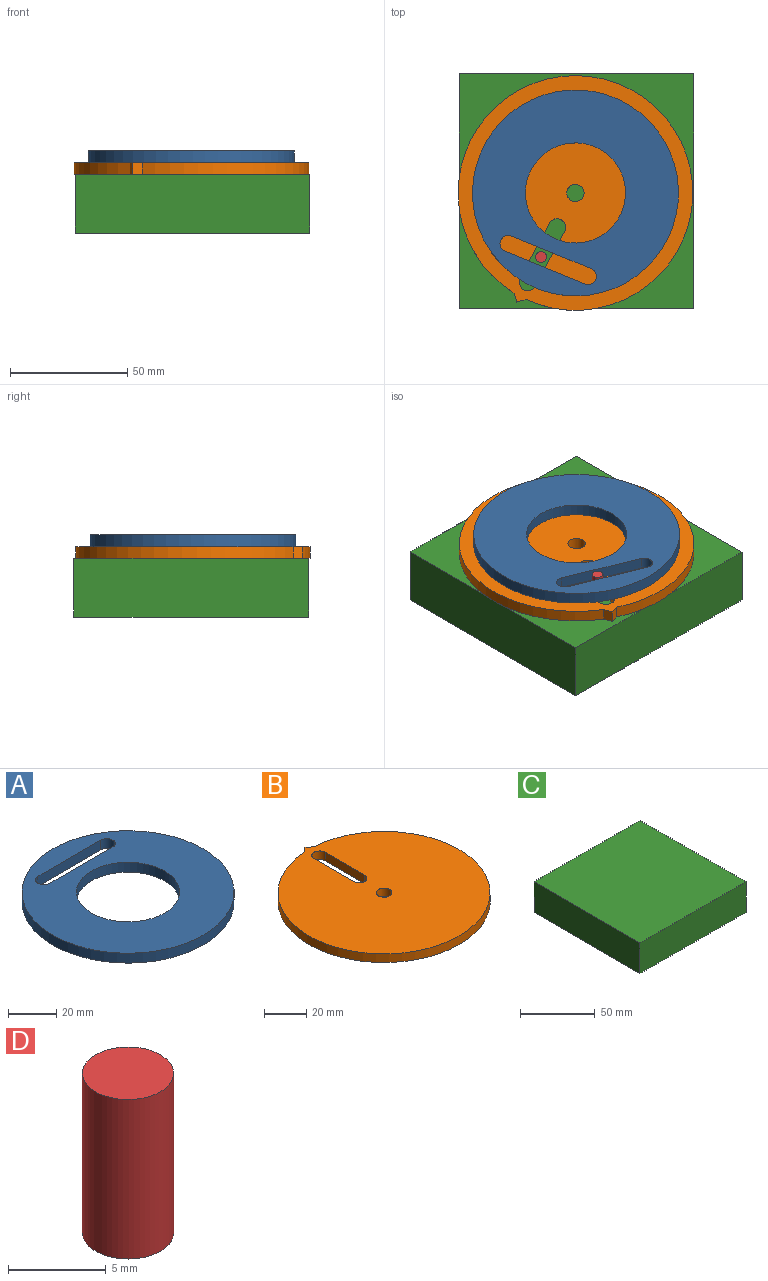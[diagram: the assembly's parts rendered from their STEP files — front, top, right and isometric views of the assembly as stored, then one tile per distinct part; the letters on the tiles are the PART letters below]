
ASSEMBLY  parts=4 mates=4
PART A: 8 faces, bbox 87.7x87.7x5 mm
  f0: cylinder r=3.5mm len=7mm, axis (0,0,-1), area 55mm2, adj f1,f4,f6,f7
  f1: plane 36.75x5mm, normal (0,-1,0), area 183.7mm2, adj f0,f2,f6,f7
  f2: cylinder r=3.5mm len=7mm, axis (0,0,-1), area 55mm2, adj f1,f4,f6,f7
  f3: cylinder r=43.87mm len=87.75mm, axis (0,0,-1), area 1378.3mm2, adj f6,f7
  f4: plane 36.75x5mm, normal (0,1,0), area 183.7mm2, adj f0,f2,f6,f7
  f5: cylinder r=21.33mm len=42.67mm, axis (0,0,-1), area 670.2mm2, adj f6,f7
  f6: plane 87.75x87.75mm, normal (0,0,1), area 4321.8mm2, adj f0,f1,f2,f3,f4,f5
  f7: plane 87.75x87.75mm, normal (0,0,-1), area 4321.8mm2, adj f0,f1,f2,f3,f4,f5
PART B: 10 faces, bbox 100x102.7x5 mm
  f0: cylinder r=50mm len=100mm, axis (0,0,-1), area 1541.8mm2, adj f1,f7,f8,f9
  f1: plane 5x2.89mm, normal (0.69,0.72,0), area 20.1mm2, adj f0,f7,f8,f9
  f2: plane 26.36x5mm, normal (1,0,0), area 131.8mm2, adj f3,f6,f8,f9
  f3: cylinder r=3.69mm len=7.37mm, axis (0,0,-1), area 57.9mm2, adj f2,f4,f8,f9
  f4: plane 26.36x5mm, normal (-1,0,0), area 131.8mm2, adj f3,f6,f8,f9
  f5: cylinder r=3.69mm len=7.37mm, axis (0,0,-1), area 115.8mm2, adj f8,f9
  f6: cylinder r=3.69mm len=7.37mm, axis (0,0,-1), area 57.9mm2, adj f2,f4,f8,f9
  f7: plane 5x2.89mm, normal (-0.69,0.72,0), area 20.1mm2, adj f0,f1,f8,f9
  f8: plane 102.71x100mm, normal (0,0,1), area 7581.9mm2, adj f0,f1,f2,f3,f4,f5,f6,f7
  f9: plane 102.71x100mm, normal (0,0,-1), area 7581.9mm2, adj f0,f1,f2,f3,f4,f5,f6,f7
PART C: 6 faces, bbox 100x100x25 mm
  f0: plane 100x25mm, normal (-1,0,0), area 2500mm2, adj f1,f3,f4,f5
  f1: plane 100x25mm, normal (0,1,0), area 2500mm2, adj f0,f2,f4,f5
  f2: plane 100x25mm, normal (1,0,0), area 2500mm2, adj f1,f3,f4,f5
  f3: plane 100x25mm, normal (0,-1,0), area 2500mm2, adj f0,f2,f4,f5
  f4: plane 100x100mm, normal (0,0,-1), area 10000mm2, adj f0,f1,f2,f3
  f5: plane 100x100mm, normal (0,0,1), area 10000mm2, adj f0,f1,f2,f3
PART D: 3 faces, bbox 4.7x4.7x10 mm
  f0: plane 4.67x4.67mm, normal (0,0,1), area 17.1mm2, adj f1
  f1: cylinder r=2.34mm len=10mm, axis (0,0,-1), area 146.8mm2, adj f0,f2
  f2: plane 4.67x4.67mm, normal (0,0,-1), area 17.1mm2, adj f1
PLACE A rot(axis=(0,0,1),157.8deg) t=(-37.82,36.21,-23.65)mm
PLACE B rot(axis=(0,0,1),151.8deg) t=(-37.82,36.21,-23.65)mm
PLACE C t=(-37.41,36.98,-23.65)mm fixed
PLACE D rot(axis=(0,0,-1),40.9deg) t=(-72.49,-14.18,-23.65)mm
MATE pin_slot D.f1 <-> B.f3  axis (0,0,-1) through (-52.49,8.9,-23.65)mm
MATE revolute C.f5 <-> B.f9  axis (0,0,1) through (-37.41,36.98,-23.65)mm
MATE pin_slot D.f1 <-> A.f2  axis (0,0,-1) through (-52.49,8.9,-13.65)mm
MATE revolute B.f0 <-> A.f5  axis (0,0,1) through (-37.82,36.21,-18.65)mm
